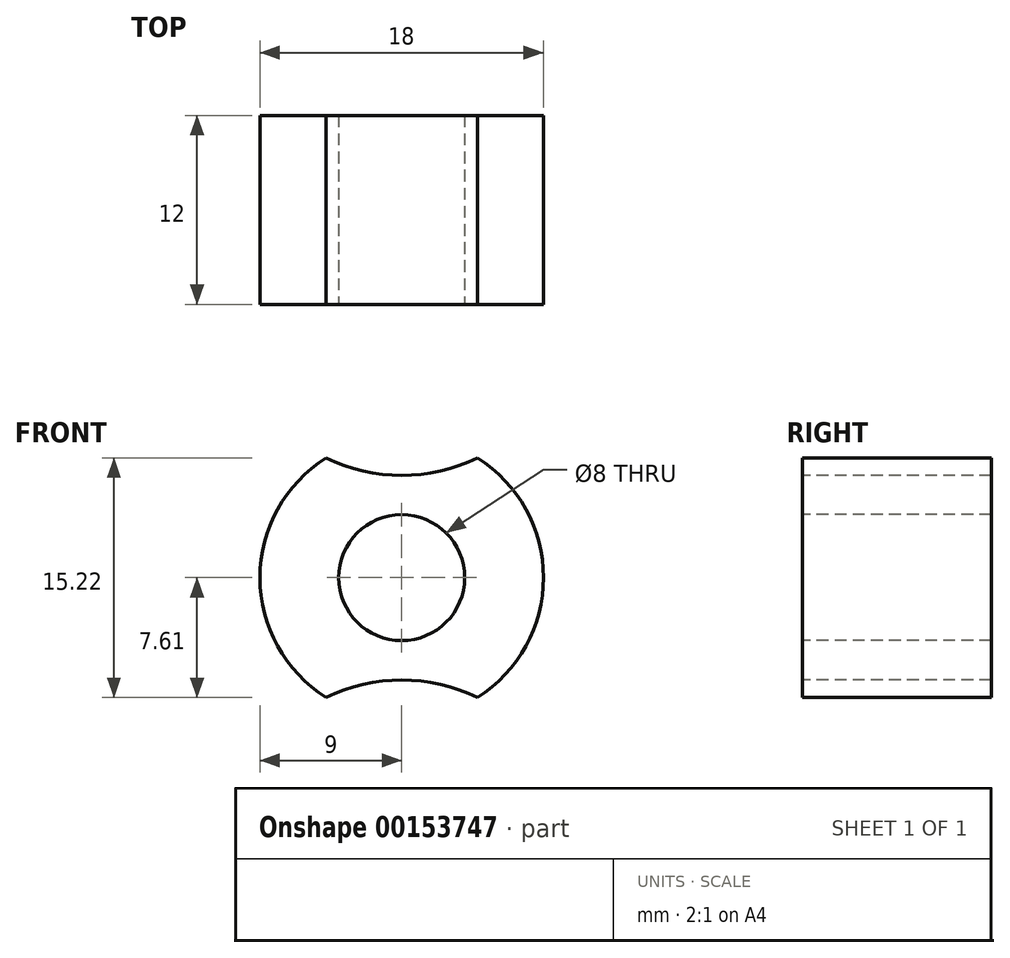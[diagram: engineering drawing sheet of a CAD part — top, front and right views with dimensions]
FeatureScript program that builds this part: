
annotation { "Feature Type Name" : "Feature", "Feature Type Description" : "" }
export const myFeature = defineFeature(function(context is Context, id is Id, definition is map)
    precondition{}
    {
        {
            var Q0;
            Q0=qCreatedBy(makeId("Front.planeOp"),FACE);
            var sketch = newSketch(context, id + "F0", { "sketchPlane" : qUnion([Q0])});
            skArc(sketch, "E0", {"start": v(-4.8, 7.6) * mm, "mid": v(-9, 0) * mm, "end": v(-4.8, -7.6) * mm});
            skCircle(sketch, "E1", {"center": v(0, 0) * mm, "radius": 4 * mm});
            skArc(sketch, "E2", {"start": v(-4.8, 7.6) * mm, "mid": v(0, 6.5) * mm, "end": v(4.8, 7.6) * mm});
            skArc(sketch, "E3", {"start": v(4.8, -7.6) * mm, "mid": v(0, -6.5) * mm, "end": v(-4.8, -7.6) * mm});
            skArc(sketch, "E4.trimOffspring", {"start": v(4.8, -7.6) * mm, "mid": v(9, 0) * mm, "end": v(4.8, 7.6) * mm});
            skSolve(sketch);
        }
        {
            var Q0;
            Q0=makeQuery(id+"F0.imprint","IMPRINT",FACE,{"disambiguationData":[TD([[makeQuery(id+"F0.imprint","IMPRINT",EDGE,{"derivedFrom":sQuery(id+"F0.wireOp",EDGE,"E0")}),1.0]])]});
            extrude(context, id + "F1", {"entities" : qUnion([Q0]), "oppositeDirection" : true, "depth" : 12 * mm});
        }
    });
